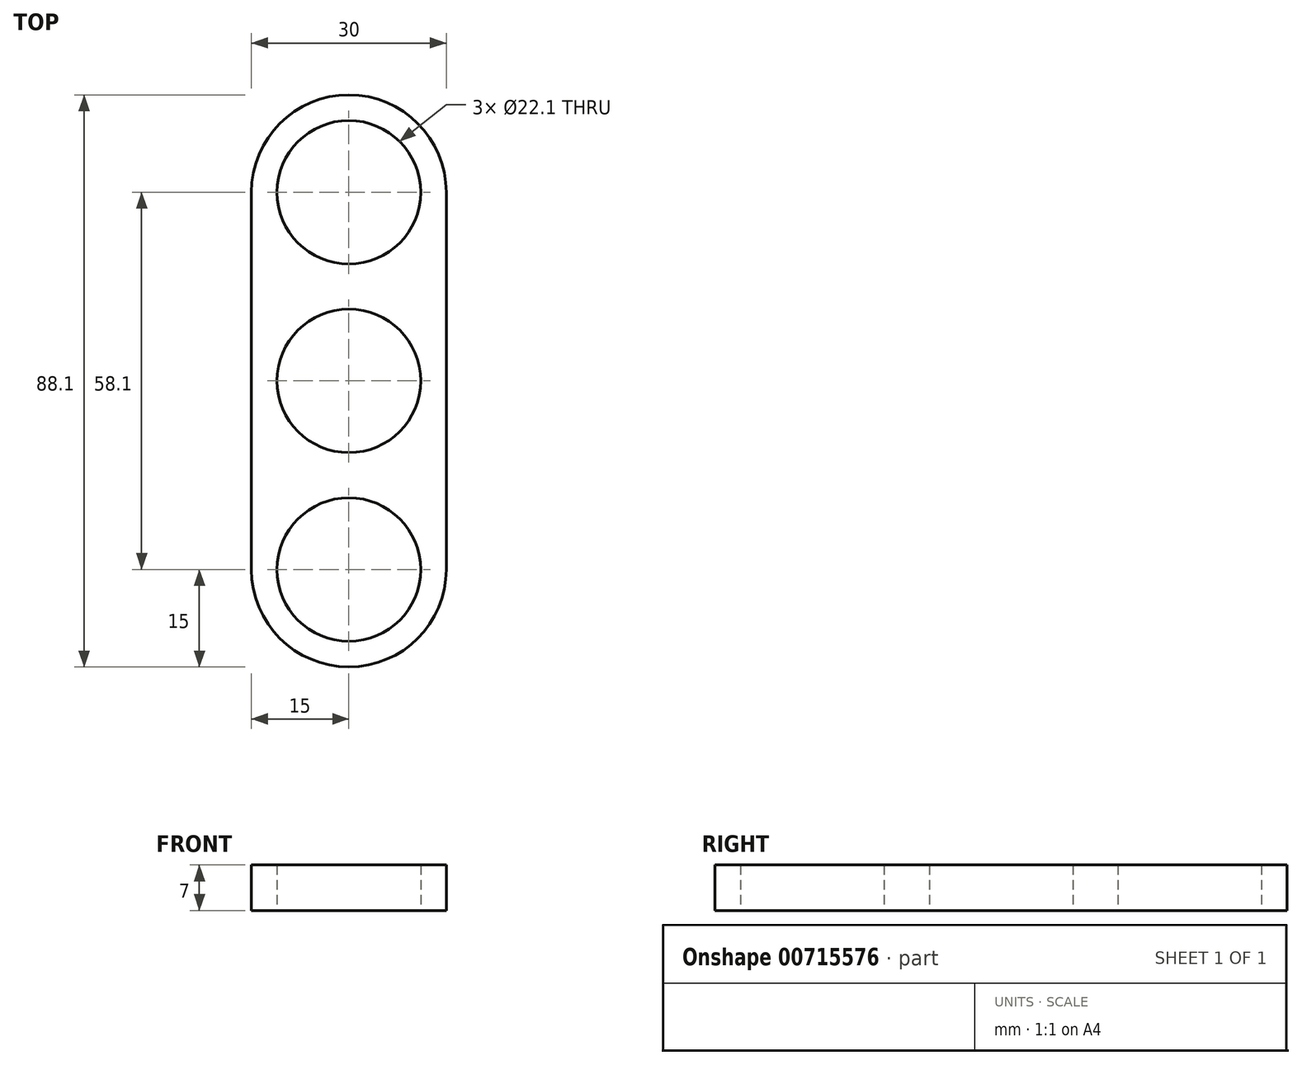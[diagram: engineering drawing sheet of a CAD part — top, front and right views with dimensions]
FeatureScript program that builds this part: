
annotation { "Feature Type Name" : "Feature", "Feature Type Description" : "" }
export const myFeature = defineFeature(function(context is Context, id is Id, definition is map)
    precondition{}
    {
        {
            var Q0;
            Q0=qCreatedBy(makeId("Top.planeOp"),FACE);
            var sketch = newSketch(context, id + "F0", { "sketchPlane" : qUnion([Q0])});
            skCircle(sketch, "E0", {"center": v(0, 0) * mm, "radius": 11.05 * mm});
            skCircle(sketch, "E1", {"center": v(0, 0) * mm, "radius": 15 * mm});
            skLineSegment(sketch, "E2", {"start": v(0, 11.05) * mm, "end": v(0, 29.05) * mm, "construction": true});
            skCircle(sketch, "E3", {"center": v(0, 29.05) * mm, "radius": 11.05 * mm});
            skArc(sketch, "E4", {"start": v(15, 29.05) * mm, "mid": v(0, 44.05) * mm, "end": v(-15, 29.05) * mm});
            skLineSegment(sketch, "E5", {"start": v(-15, 29.05) * mm, "end": v(-15, 0) * mm});
            skLineSegment(sketch, "E6", {"start": v(15, 29.05) * mm, "end": v(15, 0) * mm});
            skSolve(sketch);
        }
        {
            var Q0;
            Q0=makeQuery(id+"F0.imprint","IMPRINT",FACE,{"disambiguationData":[TD([[makeQuery(id+"F0.imprint","IMPRINT",EDGE,{"derivedFrom":sQuery(id+"F0.wireOp",EDGE,"E0")}),-1.0]])]});
            extrude(context, id + "F1", {"entities" : qUnion([Q0]), "depth" : 7 * mm, "offsetDistance" : 25 * mm});
        }
        {
            var Q0;
            Q0=makeQuery(id+"F0.imprint","IMPRINT",FACE,{"disambiguationData":[TD([[makeQuery(id+"F0.imprint","IMPRINT",EDGE,{"derivedFrom":sQuery(id+"F0.wireOp",EDGE,"E3")}),-1.0]])]});
            var Q1;
            Q1=makeQuery(id+"F1.opExtrude","CAP_FACE",FACE,{"disambiguationData":[OSD([sQuery(id+"F0.wireOp",EDGE,"E0"),sQuery(id+"F0.wireOp",EDGE,"E1")])],"isStart":false});
            extrude(context, id + "F2", {"entities" : qUnion([Q0]), "endBound" : BoundingType.UP_TO_SURFACE, "depth" : 7 * mm, "endBoundEntityFace" : qUnion([Q1]), "offsetDistance" : 25 * mm});
        }
        {
            var Q0;
            Q0=makeQuery(id+"F2.opExtrude","SWEPT_BODY",BODY,{"disambiguationData":[OSD([sQuery(id+"F0.wireOp",EDGE,"E1"),sQuery(id+"F0.wireOp",EDGE,"CE7iordk-B4aJ-mwoM-Z50K-Uj53kdkYJuOX"),sQuery(id+"F0.wireOp",EDGE,"dCJi832k-DSTx-726T-LqWB-MVPZX2p0Iy6B"),sQuery(id+"F0.wireOp",EDGE,"wBJsHTgx-hzOk-doOA-7pFN-LBJPQJBNncD7"),sQuery(id+"F0.wireOp",EDGE,"oGLxF8Ai-LGoD-j6e2-l8IM-TueIIe3S4C4U")])]});
            var Q1;
            Q1=sQuery(id+"F0.wireOp",EDGE,"E1");
            circularPattern(context, id + "F3", {"operationType" : NewBodyOperationType.ADD, "entities" : qUnion([Q0]), "axis" : qUnion([Q1]), "angle" : 360 * degree, "instanceCount" : 2, "equalSpace" : true});
        }
    });
